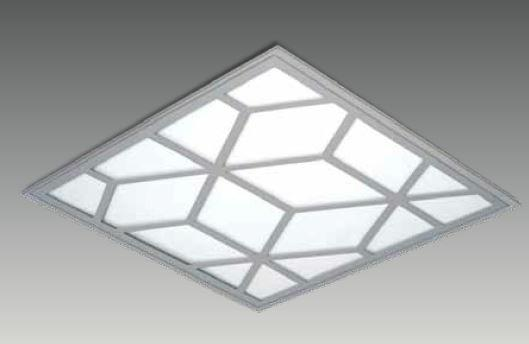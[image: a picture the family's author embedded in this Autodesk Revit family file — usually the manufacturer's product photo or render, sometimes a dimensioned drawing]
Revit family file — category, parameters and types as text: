
# Revit family: G 6060 CUB
name_source: partatom
category: Lighting Fixtures
revit_build: Autodesk Revit 2017 (Build: 20160225_1515(x64)
units: mm (PartAtom-declared; Revit-internal decimal feet)

## family parameters
Always vertical = Yes
Cut with Voids When Loaded = No
Host = Ceiling
Light Source = Yes
OmniClass Number = 23.80.70.11
OmniClass Title = Luminaries for Internal Lighting
Part Type = Normal
Room Calculation Point = No
Round Connector Dimension = Use Diameter
Shared = No

## types (4) — shared parameters
Color Filter = 16777215
Dimming Lamp Color Temperature Shift = <None>
Emit Shape Visible in Rendering = Yes
Emit from Rectangle Length = 570 mm  [stored 1.87008 ft]
Emit from Rectangle Width = 570 mm  [stored 1.87008 ft]
Light Source Symbol Size = 610 mm
Manufacturer = ARLIGHT
Type Image = G 6060 CUB.JPG

## per-type parameters (varying)
| type | Wattage Comments |
| GCUB.6060.36.30 | 36 |
| GCUB.6060.36.40 | 36 |
| GCUB.6060.28.30 | 28 |
| GCUB.6060.28.40 | 28W |

note: [stored X ft] marks values corroborated as IEEE doubles in the binary element streams (Revit-internal decimal feet)

## geometry (parser evidence)
native form markers: Sweep x2
no freeform markers — native parametric forms only
